annotation { "Feature Type Name" : "Feature", "Feature Type Description" : "" }
export const myFeature = defineFeature(function(context is Context, id is Id, definition is map)
    precondition{}
    {
        {
            var Q0;
            Q0=qCreatedBy(makeId("Front.planeOp"),FACE);
            var sketch = newSketch(context, id + "F0", { "sketchPlane" : qUnion([Q0])});
            skLineSegment(sketch, "E0.bottom", {"start": v(50.8, 9.52) * mm, "end": v(-50.8, 9.52) * mm});
            skLineSegment(sketch, "E0.top", {"start": v(50.8, -9.53) * mm, "end": v(-50.8, -9.53) * mm});
            skLineSegment(sketch, "E0.left", {"start": v(50.8, 9.52) * mm, "end": v(50.8, -9.53) * mm});
            skLineSegment(sketch, "E0.right", {"start": v(-50.8, 9.52) * mm, "end": v(-50.8, -9.53) * mm});
            skPoint(sketch, "E0.middle", {"position": v(0, 0) * mm});
            skSolve(sketch);
        }
        {
            var Q0;
            Q0 = qSketchRegion(id + "F0", true);
            var Q1;
            Q1=makeQuery(id+"F0.imprint","IMPRINT",FACE,{"disambiguationData":[TD([[makeQuery(id+"F0.imprint","IMPRINT",EDGE,{"derivedFrom":sQuery(id+"F0.wireOp",EDGE,"E0.bottom")}),1.0]])]});
            extrude(context, id + "F1", {"entities" : qUnion([Q0, Q1]), "depth" : 2.54 * mm, "offsetDistance" : 25.4 * mm});
        }
        {
            var Q0;
            Q0=makeQuery(id+"F1.opExtrude","CAP_FACE",FACE,{"disambiguationData":[OSD([sQuery(id+"F0.wireOp",EDGE,"E0.bottom"),sQuery(id+"F0.wireOp",EDGE,"E0.top"),sQuery(id+"F0.wireOp",EDGE,"E0.left"),sQuery(id+"F0.wireOp",EDGE,"E0.right")])],"isStart":false});
            var sketch = newSketch(context, id + "F2", { "sketchPlane" : qUnion([Q0])});
            skText(sketch, "E1", { "text": "DIVORCE COURT\n", "fontName": "OpenSans-Regular.ttf"});
            skLineSegment(sketch, "E2", {"start": v(40.82, 0) * mm, "end": v(44.27, 3.46) * mm});
            skLineSegment(sketch, "E3", {"start": v(44.27, 3.46) * mm, "end": v(47.73, 0) * mm});
            skLineSegment(sketch, "E4", {"start": v(47.73, 0) * mm, "end": v(44.27, -3.46) * mm});
            skLineSegment(sketch, "E5", {"start": v(44.27, -3.46) * mm, "end": v(40.82, 0) * mm});
            skLineSegment(sketch, "E6", {"start": v(-42.6, 2.44) * mm, "end": v(-44.48, 1.28) * mm});
            skLineSegment(sketch, "E7", {"start": v(-44.48, 1.28) * mm, "end": v(-40.5, -5.16) * mm});
            skLineSegment(sketch, "E8", {"start": v(-40.5, -5.16) * mm, "end": v(-43.16, -6.8) * mm});
            skLineSegment(sketch, "E9", {"start": v(-43.16, -6.8) * mm, "end": v(-47.14, -0.37) * mm});
            skLineSegment(sketch, "E10", {"start": v(-47.14, -0.37) * mm, "end": v(-49.03, -1.54) * mm});
            skLineSegment(sketch, "E11", {"start": v(-49.03, -1.54) * mm, "end": v(-48.43, 5.04) * mm});
            skLineSegment(sketch, "E12", {"start": v(-48.43, 5.04) * mm, "end": v(-42.6, 2.44) * mm});
            const initialGuessF2  = {"E1": [-0.03848, -0.00337, 1, 0, 0.00702]};
            skSetInitialGuess(sketch, initialGuessF2);
            skSolve(sketch);
        }
        {
            var Q0;
            Q0 = qSketchRegion(id + "F2", true);
            extrude(context, id + "F3", {"entities" : qUnion([Q0]), "operationType" : NewBodyOperationType.ADD, "depth" : 0.25 * mm, "offsetDistance" : 25.4 * mm});
        }
        {
            var Q0;
            Q0=makeQuery(id+"F1.opExtrude","CAP_FACE",FACE,{"disambiguationData":[OSD([sQuery(id+"F0.wireOp",EDGE,"E0.bottom"),sQuery(id+"F0.wireOp",EDGE,"E0.top"),sQuery(id+"F0.wireOp",EDGE,"E0.left"),sQuery(id+"F0.wireOp",EDGE,"E0.right")])],"isStart":true});
            var sketch = newSketch(context, id + "F4", { "sketchPlane" : qUnion([Q0])});
            skLineSegment(sketch, "E13", {"start": v(-6.35, 9.52) * mm, "end": v(-6.35, -117.48) * mm});
            skLineSegment(sketch, "E14", {"start": v(6.35, 9.52) * mm, "end": v(6.35, -117.48) * mm});
            skLineSegment(sketch, "E15", {"start": v(-6.35, -117.48) * mm, "end": v(0, -142.88) * mm});
            skLineSegment(sketch, "E16", {"start": v(0, -142.88) * mm, "end": v(6.35, -117.47) * mm});
            skSolve(sketch);
        }
        {
            var Q0;
            {var subQ0=sQuery(id+"F4.wireOp",EDGE,"E13");var subQ1=makeQuery(id+"F1.opExtrude","CAP_EDGE",EDGE,{"disambiguationData":[OSD([sQuery(id+"F0.wireOp",EDGE,"E0.bottom")])],"isStart":true});var subQ2=makeQuery(id+"F4.imprint","INTERSECT",VERTEX,{"derivedFrom":[subQ1,subQ0]});Q0=makeQuery(id+"F4.imprint","IMPRINT",FACE,{"disambiguationData":[TD([[makeQuery(id+"F4.imprint","IMPRINT",EDGE,{"disambiguationData":[TD([[subQ2,-1.0]])],"derivedFrom":subQ0}),1.0]])]});}
            var Q1;
            {var subQ1=sQuery(id+"F4.wireOp",EDGE,"E15");Q1=makeQuery(id+"F4.imprint","IMPRINT",FACE,{"disambiguationData":[TD([[makeQuery(id+"F4.imprint","IMPRINT",EDGE,{"derivedFrom":subQ1}),1.0]])]});}
            extrude(context, id + "F5", {"entities" : qUnion([Q0, Q1]), "operationType" : NewBodyOperationType.ADD, "depth" : 12.7 * mm, "offsetDistance" : 25.4 * mm});
        }
    });